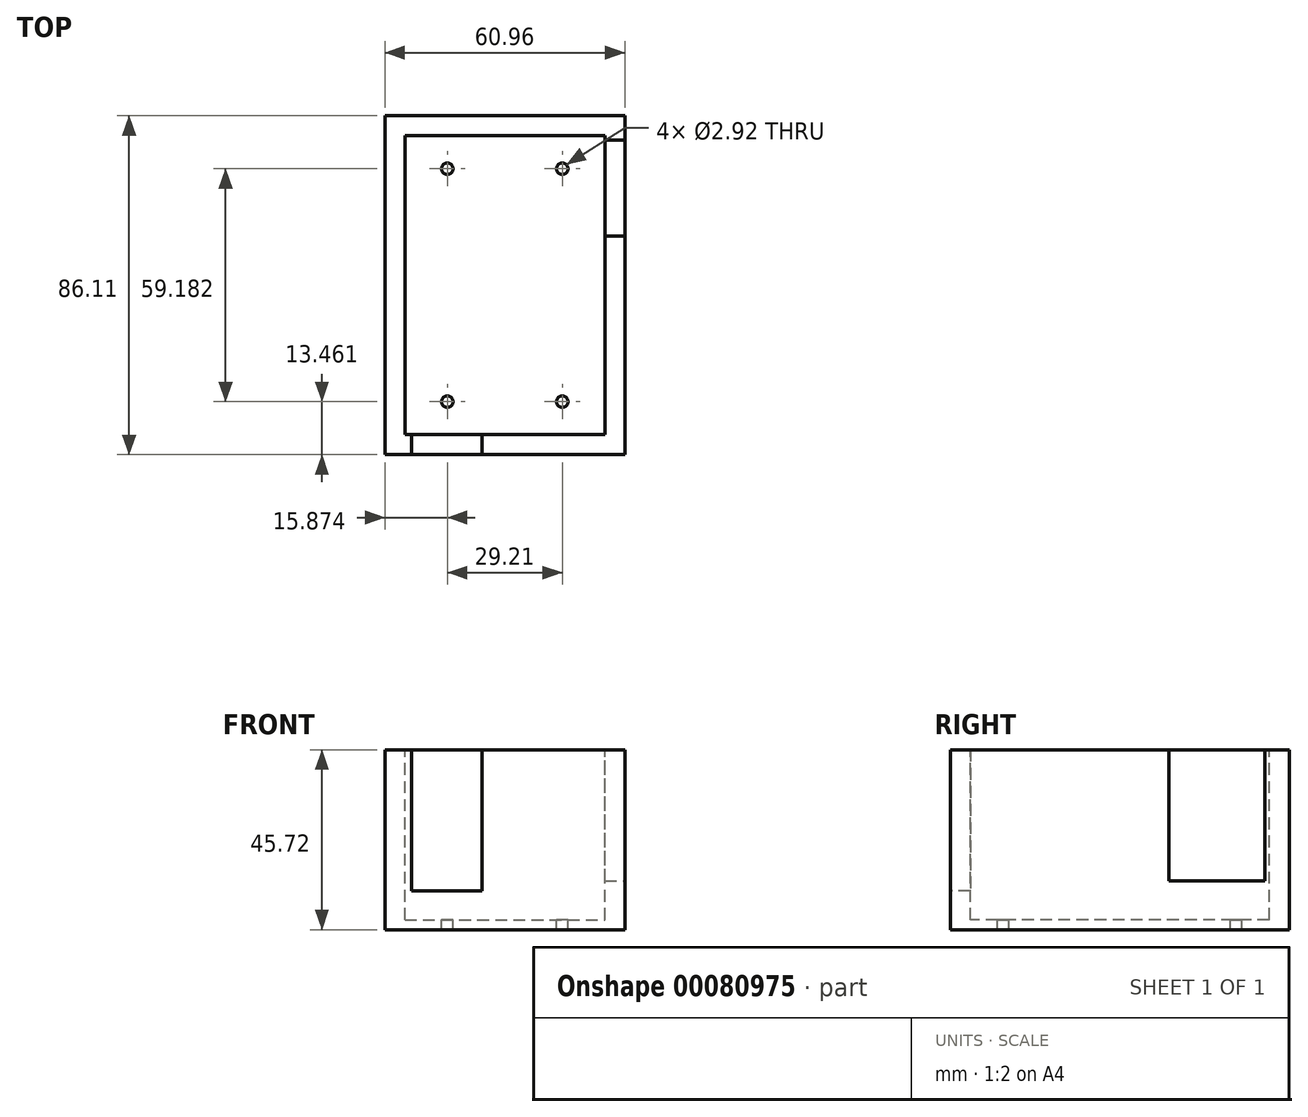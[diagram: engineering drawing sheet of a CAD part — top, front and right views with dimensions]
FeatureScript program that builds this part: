
annotation { "Feature Type Name" : "Feature", "Feature Type Description" : "" }
export const myFeature = defineFeature(function(context is Context, id is Id, definition is map)
    precondition{}
    {
        {
            var Q0;
            Q0=qCreatedBy(makeId("Top.planeOp"),FACE);
            var sketch = newSketch(context, id + "F0", { "sketchPlane" : qUnion([Q0])});
            skLineSegment(sketch, "E0.bottom", {"start": v(-24.67, 54.06) * mm, "end": v(36.29, 54.06) * mm});
            skLineSegment(sketch, "E0.top", {"start": v(-24.67, -32.05) * mm, "end": v(36.29, -32.05) * mm});
            skLineSegment(sketch, "E0.left", {"start": v(-24.67, 54.06) * mm, "end": v(-24.67, -32.05) * mm});
            skLineSegment(sketch, "E0.right", {"start": v(36.29, 54.06) * mm, "end": v(36.29, -32.05) * mm});
            skLineSegment(sketch, "E1", {"start": v(36.29, -32.05) * mm, "end": v(36.29, -23.52) * mm});
            skLineSegment(sketch, "E2.bottom", {"start": v(36.29, -23.52) * mm, "end": v(15.6, -23.52) * mm});
            skLineSegment(sketch, "E2.top", {"start": v(36.29, -32.05) * mm, "end": v(15.6, -32.05) * mm});
            skLineSegment(sketch, "E2.left", {"start": v(36.29, -23.52) * mm, "end": v(36.29, -32.05) * mm});
            skLineSegment(sketch, "E2.right", {"start": v(15.6, -23.52) * mm, "end": v(15.6, -32.05) * mm});
            skSolve(sketch);
        }
        {
            var Q0;
            Q0 = qSketchRegion(id + "F0", true);
            extrude(context, id + "F1", {"entities" : qUnion([Q0]), "depth" : 45.72 * mm});
        }
        {
            var Q0;
            Q0=makeQuery(id+"F1.opExtrude","CAP_FACE",FACE,{"disambiguationData":[OSD([sQuery(id+"F0.wireOp",EDGE,"E0.bottom"),sQuery(id+"F0.wireOp",EDGE,"E0.top"),sQuery(id+"F0.wireOp",EDGE,"E0.left"),sQuery(id+"F0.wireOp",EDGE,"E0.right"),sQuery(id+"F0.wireOp",EDGE,"E2.top"),sQuery(id+"F0.wireOp",EDGE,"E2.left")])],"isStart":false});
            var sketch = newSketch(context, id + "F2", { "sketchPlane" : qUnion([Q0])});
            skLineSegment(sketch, "E3.bottom", {"start": v(-19.6, 48.98) * mm, "end": v(31.2, 48.98) * mm});
            skLineSegment(sketch, "E3.top", {"start": v(-19.6, -26.97) * mm, "end": v(31.2, -26.97) * mm});
            skLineSegment(sketch, "E3.left", {"start": v(-19.6, 48.98) * mm, "end": v(-19.6, -26.97) * mm});
            skLineSegment(sketch, "E3.right", {"start": v(31.2, 48.98) * mm, "end": v(31.2, -26.97) * mm});
            skLineSegment(sketch, "E4", {"start": v(5.8, 48.98) * mm, "end": v(5.8, 54.06) * mm});
            skLineSegment(sketch, "E5", {"start": v(31.2, 11) * mm, "end": v(36.29, 11) * mm});
            skLineSegment(sketch, "E6", {"start": v(-19.6, 11) * mm, "end": v(-24.67, 11) * mm});
            skLineSegment(sketch, "E7", {"start": v(5.8, -26.97) * mm, "end": v(5.8, -32.05) * mm});
            skSolve(sketch);
        }
        {
            var Q0;
            {var subQ4=sQuery(id+"F2.wireOp",EDGE,"E3.left");var subQ6=sQuery(id+"F2.wireOp",EDGE,"E3.bottom");var subQ9=makeQuery(id+"F2.imprint","INTERSECT",VERTEX,{"derivedFrom":[subQ6,subQ4]});Q0=makeQuery(id+"F2.imprint","IMPRINT",FACE,{"disambiguationData":[TD([[makeQuery(id+"F2.imprint","IMPRINT",EDGE,{"disambiguationData":[TD([[subQ9,-1.0]])],"derivedFrom":subQ6}),-1.0]])]});}
            extrude(context, id + "F3", {"entities" : qUnion([Q0]), "operationType" : NewBodyOperationType.REMOVE, "oppositeDirection" : true, "depth" : 43.18 * mm});
        }
        {
            var Q0;
            Q0=makeQuery(id+"F3.boolean.opBoolean","COPY",FACE,{"derivedFrom":makeQuery(id+"F3.opExtrude","CAP_FACE",FACE,{"disambiguationData":[OSD([sQuery(id+"F2.wireOp",EDGE,"E3.bottom"),sQuery(id+"F2.wireOp",EDGE,"E3.top"),sQuery(id+"F2.wireOp",EDGE,"E3.left"),sQuery(id+"F2.wireOp",EDGE,"E3.right")])],"isStart":false})});
            var sketch = newSketch(context, id + "F4", { "sketchPlane" : qUnion([Q0])});
            skPoint(sketch, "E8.endSnap0", {"position": v(5.8, 48.98) * mm});
            skLineSegment(sketch, "E9", {"start": v(-19.6, 48.98) * mm, "end": v(-19.6, -26.97) * mm});
            skLineSegment(sketch, "E10", {"start": v(-19.6, -26.97) * mm, "end": v(31.2, -26.97) * mm});
            skLineSegment(sketch, "E11.bottom", {"start": v(-19.6, -26.97) * mm, "end": v(-8.8, -26.97) * mm});
            skLineSegment(sketch, "E11.top", {"start": v(-19.6, -18.59) * mm, "end": v(-8.8, -18.59) * mm});
            skLineSegment(sketch, "E11.left", {"start": v(-19.6, -26.97) * mm, "end": v(-19.6, -18.59) * mm});
            skLineSegment(sketch, "E11.right", {"start": v(-8.8, -26.97) * mm, "end": v(-8.8, -18.59) * mm});
            skCircle(sketch, "E12", {"center": v(-8.8, -18.59) * mm, "radius": 1.46 * mm});
            skLineSegment(sketch, "E13.bottom", {"start": v(31.2, -26.97) * mm, "end": v(20.41, -26.97) * mm});
            skLineSegment(sketch, "E13.top", {"start": v(31.2, -18.59) * mm, "end": v(20.41, -18.59) * mm});
            skLineSegment(sketch, "E13.left", {"start": v(31.2, -26.97) * mm, "end": v(31.2, -18.59) * mm});
            skLineSegment(sketch, "E13.right", {"start": v(20.41, -26.97) * mm, "end": v(20.41, -18.59) * mm});
            skCircle(sketch, "E14", {"center": v(20.41, -18.59) * mm, "radius": 1.46 * mm});
            skLineSegment(sketch, "E15", {"start": v(-8.8, -18.59) * mm, "end": v(20.41, -18.59) * mm});
            skLineSegment(sketch, "E16.bottom", {"start": v(-19.6, 40.6) * mm, "end": v(-8.8, 40.6) * mm});
            skLineSegment(sketch, "E16.top", {"start": v(-19.6, 48.98) * mm, "end": v(-8.8, 48.98) * mm});
            skLineSegment(sketch, "E16.left", {"start": v(-19.6, 40.6) * mm, "end": v(-19.6, 48.98) * mm});
            skLineSegment(sketch, "E16.right", {"start": v(-8.8, 40.6) * mm, "end": v(-8.8, 48.98) * mm});
            skLineSegment(sketch, "E17.bottom", {"start": v(31.2, 48.98) * mm, "end": v(20.41, 48.98) * mm});
            skLineSegment(sketch, "E17.top", {"start": v(31.2, 40.6) * mm, "end": v(20.41, 40.6) * mm});
            skLineSegment(sketch, "E17.left", {"start": v(31.2, 48.98) * mm, "end": v(31.2, 40.6) * mm});
            skLineSegment(sketch, "E17.right", {"start": v(20.41, 48.98) * mm, "end": v(20.41, 40.6) * mm});
            skCircle(sketch, "E18", {"center": v(-8.8, 40.6) * mm, "radius": 1.46 * mm});
            skCircle(sketch, "E19", {"center": v(20.41, 40.6) * mm, "radius": 1.46 * mm});
            skLineSegment(sketch, "E20", {"start": v(-8.8, 40.6) * mm, "end": v(20.41, 40.6) * mm});
            skLineSegment(sketch, "E21", {"start": v(20.41, 40.6) * mm, "end": v(20.41, -18.59) * mm});
            skLineSegment(sketch, "E22", {"start": v(-8.8, -18.59) * mm, "end": v(-8.8, 40.6) * mm});
            skSolve(sketch);
        }
        {
            var Q0;
            {var subQ1=sQuery(id+"F4.wireOp",EDGE,"E16.bottom");var subQ3=sQuery(id+"F4.wireOp",EDGE,"E18");var subQ4=makeQuery(id+"F4.imprint","INTERSECT",VERTEX,{"derivedFrom":[subQ1,subQ3]});Q0=makeQuery(id+"F4.imprint","IMPRINT",FACE,{"disambiguationData":[TD([[makeQuery(id+"F4.imprint","IMPRINT",EDGE,{"disambiguationData":[TD([[subQ4,-1.0]])],"derivedFrom":subQ3}),1.0]])]});}
            var Q1;
            {var subQ0=sQuery(id+"F4.wireOp",EDGE,"E20");var subQ1=sQuery(id+"F4.wireOp",EDGE,"E18");var subQ2=makeQuery(id+"F4.imprint","INTERSECT",VERTEX,{"derivedFrom":[subQ1,subQ0]});Q1=makeQuery(id+"F4.imprint","IMPRINT",FACE,{"disambiguationData":[TD([[makeQuery(id+"F4.imprint","IMPRINT",EDGE,{"disambiguationData":[TD([[subQ2,1.0]])],"derivedFrom":subQ1}),1.0]])]});}
            var Q2;
            {var subQ1=sQuery(id+"F4.wireOp",EDGE,"E16.right");var subQ3=sQuery(id+"F4.wireOp",EDGE,"E18");var subQ4=makeQuery(id+"F4.imprint","INTERSECT",VERTEX,{"derivedFrom":[subQ1,subQ3]});Q2=makeQuery(id+"F4.imprint","IMPRINT",FACE,{"disambiguationData":[TD([[makeQuery(id+"F4.imprint","IMPRINT",EDGE,{"disambiguationData":[TD([[subQ4,1.0]])],"derivedFrom":subQ3}),1.0]])]});}
            var Q3;
            {var subQ1=sQuery(id+"F4.wireOp",EDGE,"E16.bottom");var subQ3=sQuery(id+"F4.wireOp",EDGE,"E18");var subQ4=makeQuery(id+"F4.imprint","INTERSECT",VERTEX,{"derivedFrom":[subQ1,subQ3]});Q3=makeQuery(id+"F4.imprint","IMPRINT",FACE,{"disambiguationData":[TD([[makeQuery(id+"F4.imprint","IMPRINT",EDGE,{"disambiguationData":[TD([[subQ4,1.0]])],"derivedFrom":subQ3}),1.0]])]});}
            var Q4;
            {var subQ0=sQuery(id+"F4.wireOp",EDGE,"E22");var subQ1=sQuery(id+"F4.wireOp",EDGE,"E12");var subQ2=makeQuery(id+"F4.imprint","INTERSECT",VERTEX,{"derivedFrom":[subQ1,subQ0]});Q4=makeQuery(id+"F4.imprint","IMPRINT",FACE,{"disambiguationData":[TD([[makeQuery(id+"F4.imprint","IMPRINT",EDGE,{"disambiguationData":[TD([[subQ2,1.0]])],"derivedFrom":subQ1}),1.0]])]});}
            var Q5;
            {var subQ1=sQuery(id+"F4.wireOp",EDGE,"E11.top");var subQ3=sQuery(id+"F4.wireOp",EDGE,"E12");var subQ4=makeQuery(id+"F4.imprint","INTERSECT",VERTEX,{"derivedFrom":[subQ1,subQ3]});Q5=makeQuery(id+"F4.imprint","IMPRINT",FACE,{"disambiguationData":[TD([[makeQuery(id+"F4.imprint","IMPRINT",EDGE,{"disambiguationData":[TD([[subQ4,-1.0]])],"derivedFrom":subQ3}),1.0]])]});}
            var Q6;
            {var subQ1=sQuery(id+"F4.wireOp",EDGE,"E11.right");var subQ3=sQuery(id+"F4.wireOp",EDGE,"E12");var subQ4=makeQuery(id+"F4.imprint","INTERSECT",VERTEX,{"derivedFrom":[subQ1,subQ3]});Q6=makeQuery(id+"F4.imprint","IMPRINT",FACE,{"disambiguationData":[TD([[makeQuery(id+"F4.imprint","IMPRINT",EDGE,{"disambiguationData":[TD([[subQ4,-1.0]])],"derivedFrom":subQ3}),1.0]])]});}
            var Q7;
            {var subQ1=sQuery(id+"F4.wireOp",EDGE,"E11.top");var subQ3=sQuery(id+"F4.wireOp",EDGE,"E12");var subQ4=makeQuery(id+"F4.imprint","INTERSECT",VERTEX,{"derivedFrom":[subQ1,subQ3]});Q7=makeQuery(id+"F4.imprint","IMPRINT",FACE,{"disambiguationData":[TD([[makeQuery(id+"F4.imprint","IMPRINT",EDGE,{"disambiguationData":[TD([[subQ4,1.0]])],"derivedFrom":subQ3}),1.0]])]});}
            var Q8;
            {var subQ1=sQuery(id+"F4.wireOp",EDGE,"E17.top");var subQ3=sQuery(id+"F4.wireOp",EDGE,"E19");var subQ4=makeQuery(id+"F4.imprint","INTERSECT",VERTEX,{"derivedFrom":[subQ1,subQ3]});Q8=makeQuery(id+"F4.imprint","IMPRINT",FACE,{"disambiguationData":[TD([[makeQuery(id+"F4.imprint","IMPRINT",EDGE,{"disambiguationData":[TD([[subQ4,-1.0]])],"derivedFrom":subQ3}),1.0]])]});}
            var Q9;
            {var subQ1=sQuery(id+"F4.wireOp",EDGE,"E17.top");var subQ3=sQuery(id+"F4.wireOp",EDGE,"E19");var subQ4=makeQuery(id+"F4.imprint","INTERSECT",VERTEX,{"derivedFrom":[subQ1,subQ3]});Q9=makeQuery(id+"F4.imprint","IMPRINT",FACE,{"disambiguationData":[TD([[makeQuery(id+"F4.imprint","IMPRINT",EDGE,{"disambiguationData":[TD([[subQ4,1.0]])],"derivedFrom":subQ3}),1.0]])]});}
            var Q10;
            {var subQ0=sQuery(id+"F4.wireOp",EDGE,"E20");var subQ1=sQuery(id+"F4.wireOp",EDGE,"E19");var subQ2=makeQuery(id+"F4.imprint","INTERSECT",VERTEX,{"derivedFrom":[subQ1,subQ0]});Q10=makeQuery(id+"F4.imprint","IMPRINT",FACE,{"disambiguationData":[TD([[makeQuery(id+"F4.imprint","IMPRINT",EDGE,{"disambiguationData":[TD([[subQ2,-1.0]])],"derivedFrom":subQ1}),1.0]])]});}
            var Q11;
            {var subQ1=sQuery(id+"F4.wireOp",EDGE,"E17.right");var subQ3=sQuery(id+"F4.wireOp",EDGE,"E19");var subQ4=makeQuery(id+"F4.imprint","INTERSECT",VERTEX,{"derivedFrom":[subQ1,subQ3]});Q11=makeQuery(id+"F4.imprint","IMPRINT",FACE,{"disambiguationData":[TD([[makeQuery(id+"F4.imprint","IMPRINT",EDGE,{"disambiguationData":[TD([[subQ4,-1.0]])],"derivedFrom":subQ3}),1.0]])]});}
            var Q12;
            {var subQ1=sQuery(id+"F4.wireOp",EDGE,"E13.top");var subQ3=sQuery(id+"F4.wireOp",EDGE,"E14");var subQ4=makeQuery(id+"F4.imprint","INTERSECT",VERTEX,{"derivedFrom":[subQ1,subQ3]});Q12=makeQuery(id+"F4.imprint","IMPRINT",FACE,{"disambiguationData":[TD([[makeQuery(id+"F4.imprint","IMPRINT",EDGE,{"disambiguationData":[TD([[subQ4,-1.0]])],"derivedFrom":subQ3}),1.0]])]});}
            var Q13;
            {var subQ0=sQuery(id+"F4.wireOp",EDGE,"E21");var subQ1=sQuery(id+"F4.wireOp",EDGE,"E14");var subQ2=makeQuery(id+"F4.imprint","INTERSECT",VERTEX,{"derivedFrom":[subQ1,subQ0]});Q13=makeQuery(id+"F4.imprint","IMPRINT",FACE,{"disambiguationData":[TD([[makeQuery(id+"F4.imprint","IMPRINT",EDGE,{"disambiguationData":[TD([[subQ2,-1.0]])],"derivedFrom":subQ1}),1.0]])]});}
            var Q14;
            {var subQ1=sQuery(id+"F4.wireOp",EDGE,"E13.right");var subQ3=sQuery(id+"F4.wireOp",EDGE,"E14");var subQ4=makeQuery(id+"F4.imprint","INTERSECT",VERTEX,{"derivedFrom":[subQ1,subQ3]});Q14=makeQuery(id+"F4.imprint","IMPRINT",FACE,{"disambiguationData":[TD([[makeQuery(id+"F4.imprint","IMPRINT",EDGE,{"disambiguationData":[TD([[subQ4,1.0]])],"derivedFrom":subQ3}),1.0]])]});}
            var Q15;
            {var subQ1=sQuery(id+"F4.wireOp",EDGE,"E13.top");var subQ3=sQuery(id+"F4.wireOp",EDGE,"E14");var subQ4=makeQuery(id+"F4.imprint","INTERSECT",VERTEX,{"derivedFrom":[subQ1,subQ3]});Q15=makeQuery(id+"F4.imprint","IMPRINT",FACE,{"disambiguationData":[TD([[makeQuery(id+"F4.imprint","IMPRINT",EDGE,{"disambiguationData":[TD([[subQ4,1.0]])],"derivedFrom":subQ3}),1.0]])]});}
            extrude(context, id + "F5", {"entities" : qUnion([Q0, Q1, Q2, Q3, Q4, Q5, Q6, Q7, Q8, Q9, Q10, Q11, Q12, Q13, Q14, Q15]), "operationType" : NewBodyOperationType.REMOVE, "oppositeDirection" : true, "depth" : 25.4 * mm});
        }
        {
            var Q0;
            Q0=makeQuery(id+"F1.opExtrude","SWEPT_FACE",FACE,{"disambiguationData":[OSD([sQuery(id+"F0.wireOp",EDGE,"E0.right"),sQuery(id+"F0.wireOp",EDGE,"E2.left")])]});
            var sketch = newSketch(context, id + "F6", { "sketchPlane" : qUnion([Q0])});
            skLineSegment(sketch, "E23.bottom", {"start": v(23.49, 45.72) * mm, "end": v(47.88, 45.72) * mm});
            skLineSegment(sketch, "E23.top", {"start": v(23.49, 12.47) * mm, "end": v(47.88, 12.47) * mm});
            skLineSegment(sketch, "E23.left", {"start": v(23.49, 45.72) * mm, "end": v(23.49, 12.47) * mm});
            skLineSegment(sketch, "E23.right", {"start": v(47.88, 45.72) * mm, "end": v(47.88, 12.47) * mm});
            skSolve(sketch);
        }
        {
            var Q0;
            Q0=makeQuery(id+"F6.imprint","IMPRINT",FACE,{"disambiguationData":[TD([[makeQuery(id+"F6.imprint","IMPRINT",EDGE,{"derivedFrom":sQuery(id+"F6.wireOp",EDGE,"E23.bottom")}),1.0]])]});
            extrude(context, id + "F7", {"entities" : qUnion([Q0]), "operationType" : NewBodyOperationType.REMOVE, "oppositeDirection" : true, "depth" : 25.4 * mm});
        }
        {
            var Q0;
            Q0=makeQuery(id+"F1.opExtrude","SWEPT_FACE",FACE,{"disambiguationData":[OSD([sQuery(id+"F0.wireOp",EDGE,"E0.top"),sQuery(id+"F0.wireOp",EDGE,"E2.top")])]});
            var sketch = newSketch(context, id + "F8", { "sketchPlane" : qUnion([Q0])});
            skLineSegment(sketch, "E24.bottom", {"start": v(-17.83, 45.72) * mm, "end": v(0, 45.72) * mm});
            skLineSegment(sketch, "E24.top", {"start": v(-17.83, 9.86) * mm, "end": v(0, 9.86) * mm});
            skLineSegment(sketch, "E24.left", {"start": v(-17.83, 45.72) * mm, "end": v(-17.83, 9.86) * mm});
            skLineSegment(sketch, "E24.right", {"start": v(0, 45.72) * mm, "end": v(0, 9.86) * mm});
            skSolve(sketch);
        }
        {
            var Q0;
            Q0=makeQuery(id+"F8.imprint","IMPRINT",FACE,{"disambiguationData":[TD([[makeQuery(id+"F8.imprint","IMPRINT",EDGE,{"derivedFrom":sQuery(id+"F8.wireOp",EDGE,"E24.bottom")}),-1.0]])]});
            extrude(context, id + "F9", {"entities" : qUnion([Q0]), "operationType" : NewBodyOperationType.REMOVE, "oppositeDirection" : true, "depth" : 25.4 * mm});
        }
    });
